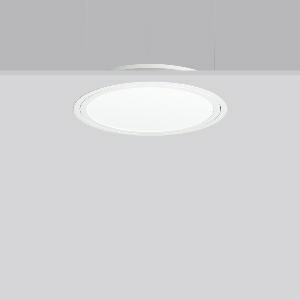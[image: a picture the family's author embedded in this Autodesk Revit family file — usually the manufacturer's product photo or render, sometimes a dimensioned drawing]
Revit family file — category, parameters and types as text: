
# Revit family: triona_round_e_312419_002_12_be88
name_source: partatom
category: Lighting Fixtures
units: mm (PartAtom-declared; Revit-internal decimal feet)

## family parameters
Cut with Voids When Loaded = No
Host = Face
Light Source = No
Part Type = Normal
Room Calculation Point = No
Round Connector Dimension = Use Diameter
Shared = No

## types (1)
- TRIONA round E (1 x LED Modul 830, 4650 lm, 3000)
    Apparent Load = 48 VA
    CIE Flux Codes = 49 80 96 100 100
    Color Rendering = 80
    Color Temperature = 3000
    Default Elevation = 1800 mm
    Description = Series: TRIONA round
Decorative round LED recessed surface luminaire. Cover made of sheet steel, powder-coated. Frame made of aluminium, powder-coated. Recessed ring: aluminium extrusion profile, powder coated. Light emission through a diffuser: plastic, opal. Lightguide and diffuser made of non-yellowing plastic (PMMA). Lateral light emission (RZB SIDELITE technology) for above-average homogeneous light distribution. Suitable for installation in cavity ceilings. Tool-free mounting system thanks to the rocker arm mechanism (patent pending). Electronic ballast included. Very easy installation thanks to Plug+Play connection. 
Colour: traffic white, matt (RAL 9016)
Diameter: 505 mm
Height: 2 mm
Cut-out diameter: 482 mm
Recess height: 100 mm
Luminaire: recess height: 89 mm
Lamp: LED
Socket: without socket
Colour temperature: 3000K
Colour rendering index (CRI): 80
System power: 48 W
Rated luminous flux: 4650 lm
Luminous efficiency: 97 lm/W
Control gear: Converter, dimmable, DALI
Protection class: I
Type of protection: IP 40
    Height = 0 mm  [stored 0 ft]
    Lamp = 1 x LED Modul 830
    Lamp Light Flux = 4650 lm
    Lamp count = 1
    Length = 505 mm
    Lifetime = 50000 h
    Luminous efficacy = 97 lm/W
    Manufacturer = RZB
    ModVariant = No
    Model = 312419.002.12
    Mounting Place = Ceiling
    Mounting Type = Recessed
    Number of Poles = 1
    OnlyDefault = Yes
    Power Factor = 1
    Product Name = TRIONA round E
    Product group = Recessed modular luminaires
    ProductGroupID = 406
    Protection Class = Protection class I
    Protection Degree = IP 20
    RLX_Detail_Level = 1
    RLX_Emergency_Light_Flux = 0 lm
    RLX_Emergency_Type = 0
    RLX_Emergency_Type_DB = No
    RlxData = <blob elided: 30129 chars, md5=5e567e14>
    Socket = socket
    Standby Power = 0 W
    System Light Flux = 4650 lm
    System Power = 48 W
    Type Comments = Product without accessories
    Type Image = 312419.002.12.jpg
    URL = http://relux.com
    VarID = ---
    Voltage = 230 V
    Voltage Range = 220-240 V
    Weight = 0.00 kg
    Width = 0 mm  [stored 0 ft]

note: [stored X ft] marks values corroborated as IEEE doubles in the binary element streams (Revit-internal decimal feet)

## geometry (parser evidence)
native form markers: Blend x4, Sweep x10
no freeform markers — native parametric forms only
